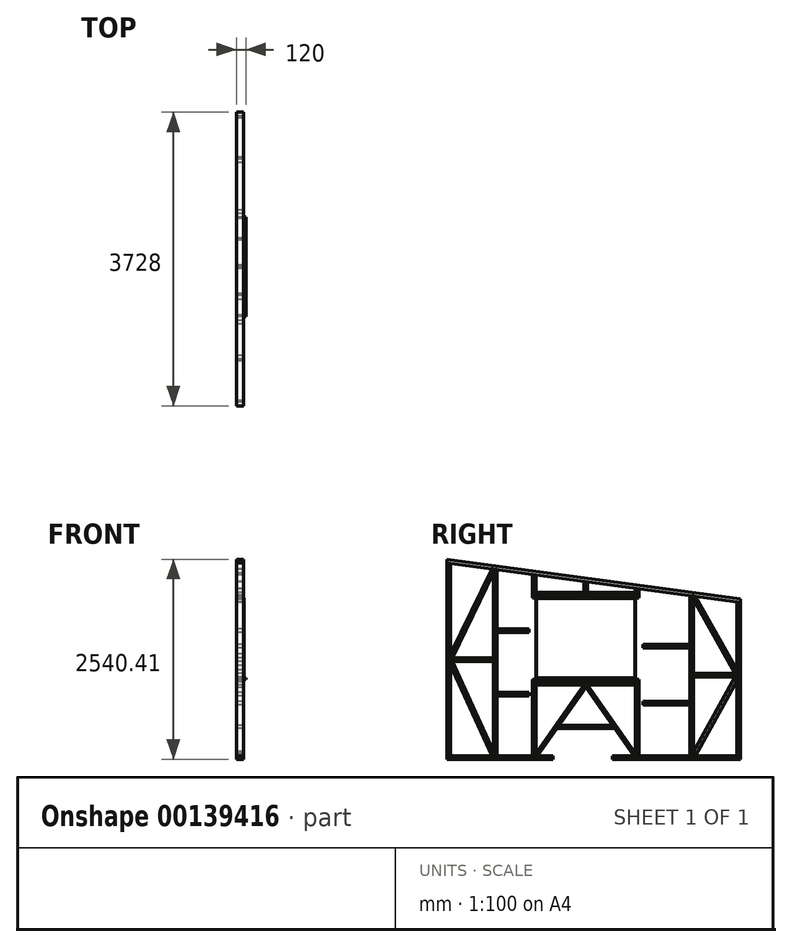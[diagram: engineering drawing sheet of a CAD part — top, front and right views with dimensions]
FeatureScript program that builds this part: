
annotation { "Feature Type Name" : "Feature", "Feature Type Description" : "" }
export const myFeature = defineFeature(function(context is Context, id is Id, definition is map)
    precondition{}
    {
        {
            var Q0;
            Q0=qCreatedBy(makeId("Right.planeOp"),FACE);
            var sketch = newSketch(context, id + "F0", { "sketchPlane" : qUnion([Q0])});
            skLineSegment(sketch, "E0.right", {"start": v(3252.07, -1561.25) * mm, "end": v(3252.07, 393.75) * mm});
            skLineSegment(sketch, "E1", {"start": v(3252.07, 393.75) * mm, "end": v(3297.07, 387.7) * mm});
            skLineSegment(sketch, "E2", {"start": v(3297.07, 387.7) * mm, "end": v(3297.07, -1561.25) * mm});
            skLineSegment(sketch, "E3", {"start": v(164.07, 808.78) * mm, "end": v(164.07, -1561.25) * mm});
            skLineSegment(sketch, "E4", {"start": v(610.07, -1561.25) * mm, "end": v(610.07, 748.84) * mm});
            skLineSegment(sketch, "E5", {"start": v(655.07, -1561.25) * mm, "end": v(655.07, 742.8) * mm});
            skLineSegment(sketch, "E6", {"start": v(610.07, 748.84) * mm, "end": v(655.07, 742.8) * mm});
            skLineSegment(sketch, "E7", {"start": v(2057.07, -1561.25) * mm, "end": v(2057.07, 554.36) * mm});
            skLineSegment(sketch, "E8", {"start": v(2012.07, -1561.25) * mm, "end": v(2012.07, 560.41) * mm});
            skLineSegment(sketch, "E9", {"start": v(2012.07, 560.41) * mm, "end": v(2057.07, 554.36) * mm});
            skLineSegment(sketch, "E10.bottom", {"start": v(655.07, 445.75) * mm, "end": v(2012.07, 445.75) * mm});
            skLineSegment(sketch, "E10.top", {"start": v(655.07, -591.25) * mm, "end": v(2012.07, -591.25) * mm});
            skLineSegment(sketch, "E10.left", {"start": v(655.07, 445.75) * mm, "end": v(655.07, -591.25) * mm});
            skLineSegment(sketch, "E10.right", {"start": v(2012.07, 445.75) * mm, "end": v(2012.07, -591.25) * mm});
            skLineSegment(sketch, "E11", {"start": v(655.07, 480.75) * mm, "end": v(2012.07, 480.75) * mm});
            skLineSegment(sketch, "E12", {"start": v(655.07, -626.25) * mm, "end": v(2012.07, -626.25) * mm});
            skLineSegment(sketch, "E13", {"start": v(655.07, -661.25) * mm, "end": v(2012.07, -661.25) * mm});
            skLineSegment(sketch, "E14", {"start": v(655.07, 515.75) * mm, "end": v(2012.07, 515.75) * mm});
            skPoint(sketch, "E15", {"position": v(1333.57, -661.25) * mm});
            skLineSegment(sketch, "E16", {"start": v(1333.57, -661.25) * mm, "end": v(1333.57, -1561.25) * mm, "construction": true});
            skLineSegment(sketch, "E17", {"start": v(1333.57, -661.25) * mm, "end": v(700.07, -1561.25) * mm, "construction": true});
            skLineSegment(sketch, "E18", {"start": v(1333.57, -661.25) * mm, "end": v(1967.07, -1561.25) * mm, "construction": true});
            skLineSegment(sketch, "E19.right", {"start": v(3297.07, -1561.25) * mm, "end": v(3297.07, -1606.25) * mm});
            skLineSegment(sketch, "E20", {"start": v(-385.93, -361.25) * mm, "end": v(164.07, -1561.25) * mm, "construction": true});
            skLineSegment(sketch, "E21", {"start": v(-361.18, -361.25) * mm, "end": v(164.07, -1507.25) * mm});
            skLineSegment(sketch, "E22", {"start": v(-385.93, -415.25) * mm, "end": v(139.32, -1561.25) * mm});
            skLineSegment(sketch, "E23", {"start": v(3297.07, 387.7) * mm, "end": v(-430.93, 888.75) * mm});
            skLineSegment(sketch, "E24", {"start": v(-430.93, 888.75) * mm, "end": v(-430.93, -1561.25) * mm});
            skLineSegment(sketch, "E25", {"start": v(-430.93, 888.75) * mm, "end": v(-430.93, 934.16) * mm});
            skLineSegment(sketch, "E26", {"start": v(-430.93, 934.16) * mm, "end": v(3297.07, 433.1) * mm});
            skLineSegment(sketch, "E27", {"start": v(3297.07, 433.1) * mm, "end": v(3297.07, 387.7) * mm});
            skLineSegment(sketch, "E28", {"start": v(164.07, -361.25) * mm, "end": v(-385.93, -361.25) * mm});
            skLineSegment(sketch, "E29", {"start": v(164.07, 808.78) * mm, "end": v(-385.93, -316.25) * mm, "construction": true});
            skLineSegment(sketch, "E30", {"start": v(140.57, 811.94) * mm, "end": v(-385.93, -265.02) * mm});
            skLineSegment(sketch, "E31", {"start": v(164.07, 757.55) * mm, "end": v(-360.89, -316.25) * mm});
            skLineSegment(sketch, "E32", {"start": v(2702.07, 467.67) * mm, "end": v(3252.07, -516.25) * mm, "construction": true});
            skLineSegment(sketch, "E33", {"start": v(3252.07, -561.25) * mm, "end": v(2702.07, -1561.25) * mm, "construction": true});
            skLineSegment(sketch, "E34", {"start": v(2729.94, 463.93) * mm, "end": v(3252.07, -470.13) * mm});
            skLineSegment(sketch, "E35", {"start": v(3226.39, -561.25) * mm, "end": v(2702.07, -1514.56) * mm});
            skLineSegment(sketch, "E36", {"start": v(3252.07, -607.94) * mm, "end": v(2727.75, -1561.25) * mm});
            skLineSegment(sketch, "E37", {"start": v(2702.07, -516.25) * mm, "end": v(3252.07, -516.25) * mm});
            skLineSegment(sketch, "E38", {"start": v(2702.07, -561.25) * mm, "end": v(3252.07, -561.25) * mm});
            skLineSegment(sketch, "E39", {"start": v(700.07, -591.25) * mm, "end": v(700.07, 445.75) * mm});
            skLineSegment(sketch, "E40", {"start": v(700.07, 515.75) * mm, "end": v(700.07, 736.74) * mm});
            skLineSegment(sketch, "E41", {"start": v(1967.07, -591.25) * mm, "end": v(1967.07, 445.75) * mm});
            skLineSegment(sketch, "E42", {"start": v(1967.07, 515.75) * mm, "end": v(1967.07, 566.46) * mm});
            skLineSegment(sketch, "E43", {"start": v(1672.07, -1561.25) * mm, "end": v(1672.07, -1606.25) * mm});
            skLineSegment(sketch, "E44", {"start": v(-430.93, -1561.25) * mm, "end": v(919.07, -1561.25) * mm});
            skLineSegment(sketch, "E45", {"start": v(1672.07, -1606.25) * mm, "end": v(3297.07, -1606.25) * mm});
            skLineSegment(sketch, "E46", {"start": v(3297.07, -1561.25) * mm, "end": v(1672.07, -1561.25) * mm});
            skLineSegment(sketch, "E47", {"start": v(919.07, -1606.25) * mm, "end": v(919.07, -1561.25) * mm});
            skLineSegment(sketch, "E48", {"start": v(3226.3, -516.25) * mm, "end": v(2702.07, 421.56) * mm});
            skLineSegment(sketch, "E49", {"start": v(1967.07, -661.25) * mm, "end": v(1967.07, -1561.25) * mm});
            skLineSegment(sketch, "E50", {"start": v(700.07, -661.25) * mm, "end": v(700.07, -1561.25) * mm});
            skLineSegment(sketch, "E51", {"start": v(1354.97, -661.25) * mm, "end": v(1967.07, -1530.84) * mm});
            skLineSegment(sketch, "E52", {"start": v(1333.57, -691.65) * mm, "end": v(1945.67, -1561.25) * mm});
            skLineSegment(sketch, "E53", {"start": v(1333.57, -691.65) * mm, "end": v(721.47, -1561.25) * mm});
            skLineSegment(sketch, "E54", {"start": v(1312.17, -661.25) * mm, "end": v(700.07, -1530.84) * mm});
            skLineSegment(sketch, "E55", {"start": v(1333.57, -691.65) * mm, "end": v(1333.57, -661.25) * mm});
            skLineSegment(sketch, "E56", {"start": v(-385.93, -1561.25) * mm, "end": v(-385.93, 882.7) * mm});
            skLineSegment(sketch, "E57", {"start": v(164.07, -316.25) * mm, "end": v(-385.93, -316.25) * mm});
            skLineSegment(sketch, "E58", {"start": v(919.07, -1606.25) * mm, "end": v(-430.93, -1606.25) * mm});
            skLineSegment(sketch, "E59", {"start": v(-430.93, -1606.25) * mm, "end": v(-430.93, -1561.25) * mm});
            skLineSegment(sketch, "E60", {"start": v(2657.07, 473.72) * mm, "end": v(2657.07, -1561.25) * mm});
            skLineSegment(sketch, "E61", {"start": v(2702.07, 467.67) * mm, "end": v(2702.07, -1561.25) * mm});
            skLineSegment(sketch, "E62", {"start": v(209.07, 802.74) * mm, "end": v(209.07, -1561.25) * mm});
            skLineSegment(sketch, "E63", {"start": v(2657.07, -192.64) * mm, "end": v(2057.07, -192.64) * mm});
            skLineSegment(sketch, "E64", {"start": v(2657.07, -147.64) * mm, "end": v(2057.07, -147.64) * mm});
            skLineSegment(sketch, "E65", {"start": v(2657.07, -913.64) * mm, "end": v(2057.07, -913.64) * mm});
            skLineSegment(sketch, "E66", {"start": v(2657.07, -868.64) * mm, "end": v(2057.07, -868.64) * mm});
            skLineSegment(sketch, "E67", {"start": v(610.07, -800.25) * mm, "end": v(209.07, -800.25) * mm});
            skLineSegment(sketch, "E68", {"start": v(610.07, -755.25) * mm, "end": v(209.07, -755.25) * mm});
            skLineSegment(sketch, "E69", {"start": v(610.07, 5.75) * mm, "end": v(209.07, 5.75) * mm});
            skLineSegment(sketch, "E70", {"start": v(610.07, 50.75) * mm, "end": v(209.07, 50.75) * mm});
            skLineSegment(sketch, "E71", {"start": v(1333.57, 515.75) * mm, "end": v(1333.57, 651.6) * mm, "construction": true});
            skLineSegment(sketch, "E72", {"start": v(1356.07, 648.58) * mm, "end": v(1356.07, 515.75) * mm});
            skLineSegment(sketch, "E73", {"start": v(1311.07, 654.63) * mm, "end": v(1311.07, 515.75) * mm});
            skLineSegment(sketch, "E74", {"start": v(992.47, -1176.25) * mm, "end": v(1674.67, -1176.25) * mm});
            skLineSegment(sketch, "E75", {"start": v(1699.3, -1211.25) * mm, "end": v(967.83, -1211.25) * mm});
            skLineSegment(sketch, "E76", {"start": v(1333.57, -661.25) * mm, "end": v(1333.57, 1002.43) * mm, "construction": true});
            skLineSegment(sketch, "E77.bottom", {"start": v(1955.07, 431.75) * mm, "end": v(712.07, 431.75) * mm});
            skLineSegment(sketch, "E77.top", {"start": v(1955.07, -566.25) * mm, "end": v(712.07, -566.25) * mm});
            skLineSegment(sketch, "E77.left", {"start": v(1955.07, 431.75) * mm, "end": v(1955.07, -566.25) * mm});
            skLineSegment(sketch, "E77.right", {"start": v(712.07, 431.75) * mm, "end": v(712.07, -566.25) * mm});
            skPoint(sketch, "E77.middle", {"position": v(1333.57, -67.25) * mm});
            skLineSegment(sketch, "E78", {"start": v(700.07, -571.25) * mm, "end": v(1967.07, -571.25) * mm});
            skLineSegment(sketch, "E79", {"start": v(700.07, 436.75) * mm, "end": v(1967.07, 436.75) * mm});
            skLineSegment(sketch, "E80", {"start": v(709.07, -591.25) * mm, "end": v(709.07, 436.75) * mm});
            skLineSegment(sketch, "E81", {"start": v(1958.07, 436.75) * mm, "end": v(1958.07, -571.25) * mm});
            skSolve(sketch);
        }
        {
            var Q0;
            {var subQ0=sQuery(id+"F0.wireOp",EDGE,"E3");var subQ5=sQuery(id+"F0.wireOp",EDGE,"E23");var subQ6=makeQuery(id+"F0.imprint","INTERSECT",VERTEX,{"derivedFrom":[subQ0,subQ5]});Q0=makeQuery(id+"F0.imprint","IMPRINT",FACE,{"disambiguationData":[TD([[makeQuery(id+"F0.imprint","IMPRINT",EDGE,{"disambiguationData":[TD([[subQ6,-1.0]])],"derivedFrom":subQ0}),1.0]])]});}
            var Q1;
            {var subQ0=sQuery(id+"F0.wireOp",EDGE,"E10.right");Q1=makeQuery(id+"F0.imprint","IMPRINT",FACE,{"disambiguationData":[TD([[makeQuery(id+"F0.imprint","IMPRINT",EDGE,{"derivedFrom":subQ0}),1.0]])]});}
            var Q2;
            {var subQ0=sQuery(id+"F0.wireOp",EDGE,"E19.bottom");var subQ5=sQuery(id+"F0.wireOp",EDGE,"f47dd481-e89d-4789-ba86-61e8c564b81a");var subQ9=makeQuery(id+"F0.imprint","INTERSECT",VERTEX,{"derivedFrom":[subQ5,subQ0]});Q2=makeQuery(id+"F0.imprint","IMPRINT",FACE,{"disambiguationData":[TD([[makeQuery(id+"F0.imprint","IMPRINT",EDGE,{"disambiguationData":[TD([[subQ9,-1.0]])],"derivedFrom":subQ5}),1.0]])]});}
            var Q3;
            {var subQ0=sQuery(id+"F0.wireOp",EDGE,"9458f50f-a9ba-4b11-8554-c1f147fb82af");var subQ3=sQuery(id+"F0.wireOp",EDGE,"E23");var subQ9=makeQuery(id+"F0.imprint","INTERSECT",VERTEX,{"derivedFrom":[subQ0,subQ3]});Q3=makeQuery(id+"F0.imprint","IMPRINT",FACE,{"disambiguationData":[TD([[makeQuery(id+"F0.imprint","IMPRINT",EDGE,{"disambiguationData":[TD([[subQ9,-1.0]])],"derivedFrom":subQ0}),-1.0]])]});}
            var Q4;
            {var subQ8=sQuery(id+"F0.wireOp",EDGE,"E1");Q4=makeQuery(id+"F0.imprint","IMPRINT",FACE,{"disambiguationData":[TD([[makeQuery(id+"F0.imprint","IMPRINT",EDGE,{"derivedFrom":subQ8}),-1.0]])]});}
            var Q5;
            {var subQ0=sQuery(id+"F0.wireOp",EDGE,"E60");var subQ8=sQuery(id+"F0.wireOp",EDGE,"E23");var subQ11=makeQuery(id+"F0.imprint","INTERSECT",VERTEX,{"derivedFrom":[subQ8,subQ0]});Q5=makeQuery(id+"F0.imprint","IMPRINT",FACE,{"disambiguationData":[TD([[makeQuery(id+"F0.imprint","IMPRINT",EDGE,{"disambiguationData":[TD([[subQ11,1.0]])],"derivedFrom":subQ8}),1.0]])]});}
            var Q6;
            {var subQ0=sQuery(id+"F0.wireOp",EDGE,"qufnCjFI-fICh-2xJd-mXJg-Tk57APwGPwlv");Q6=makeQuery(id+"F0.imprint","IMPRINT",FACE,{"disambiguationData":[TD([[makeQuery(id+"F0.imprint","IMPRINT",EDGE,{"derivedFrom":subQ0}),1.0]])]});}
            var Q7;
            {var subQ0=sQuery(id+"F0.wireOp",EDGE,"E72");Q7=makeQuery(id+"F0.imprint","IMPRINT",FACE,{"disambiguationData":[TD([[makeQuery(id+"F0.imprint","IMPRINT",EDGE,{"derivedFrom":subQ0}),-1.0]])]});}
            var Q8;
            {var subQ6=sQuery(id+"F0.wireOp",EDGE,"E2");Q8=makeQuery(id+"F0.imprint","IMPRINT",FACE,{"disambiguationData":[TD([[makeQuery(id+"F0.imprint","IMPRINT",EDGE,{"derivedFrom":subQ6}),-1.0]])]});}
            var Q9;
            {var subQ6=sQuery(id+"F0.wireOp",EDGE,"E10.left");Q9=makeQuery(id+"F0.imprint","IMPRINT",FACE,{"disambiguationData":[TD([[makeQuery(id+"F0.imprint","IMPRINT",EDGE,{"derivedFrom":subQ6}),-1.0]])]});}
            var Q10;
            {var subQ0=sQuery(id+"F0.wireOp",EDGE,"E74");Q10=makeQuery(id+"F0.imprint","IMPRINT",FACE,{"disambiguationData":[TD([[makeQuery(id+"F0.imprint","IMPRINT",EDGE,{"derivedFrom":subQ0}),-1.0]])]});}
            extrude(context, id + "F1", {"entities" : qUnion([Q0, Q1, Q2, Q3, Q4, Q5, Q6, Q7, Q8, Q9, Q10]), "depth" : 90 * mm});
        }
        {
            var Q0;
            {var subQ0=sQuery(id+"F0.wireOp",EDGE,"KPTtf08t-VQN6-3Sqd-dzWE-HS9itD71kze6");Q0=makeQuery(id+"F0.imprint","IMPRINT",FACE,{"disambiguationData":[TD([[makeQuery(id+"F0.imprint","IMPRINT",EDGE,{"derivedFrom":subQ0}),-1.0]])]});}
            var Q1;
            {var subQ7=sQuery(id+"F0.wireOp",EDGE,"E25");Q1=makeQuery(id+"F0.imprint","IMPRINT",FACE,{"disambiguationData":[TD([[makeQuery(id+"F0.imprint","IMPRINT",EDGE,{"derivedFrom":subQ7}),-1.0]])]});}
            var Q2;
            Q2=makeQuery(id+"F0.imprint","IMPRINT",FACE,{"disambiguationData":[TD([[makeQuery(id+"F0.imprint","IMPRINT",EDGE,{"derivedFrom":sQuery(id+"F0.wireOp",EDGE,"E19.top")}),1.0]])]});
            var Q3;
            {var subQ0=sQuery(id+"F0.wireOp",EDGE,"64f86141-53e5-40fa-8328-e75aae3fffb5");Q3=makeQuery(id+"F0.imprint","IMPRINT",FACE,{"disambiguationData":[TD([[makeQuery(id+"F0.imprint","IMPRINT",EDGE,{"derivedFrom":subQ0}),1.0]])]});}
            var Q4;
            {var subQ0=sQuery(id+"F0.wireOp",EDGE,"E11");Q4=makeQuery(id+"F0.imprint","IMPRINT",FACE,{"disambiguationData":[TD([[makeQuery(id+"F0.imprint","IMPRINT",EDGE,{"derivedFrom":subQ0}),1.0]])]});}
            var Q5;
            {var subQ0=sQuery(id+"F0.wireOp",EDGE,"9b8bf4e2-eade-4215-bfc9-b225c43cc35f");Q5=makeQuery(id+"F0.imprint","IMPRINT",FACE,{"disambiguationData":[TD([[makeQuery(id+"F0.imprint","IMPRINT",EDGE,{"derivedFrom":subQ0}),-1.0]])]});}
            var Q6;
            {var subQ0=sQuery(id+"F0.wireOp",EDGE,"E10.top");Q6=makeQuery(id+"F0.imprint","IMPRINT",FACE,{"disambiguationData":[TD([[makeQuery(id+"F0.imprint","IMPRINT",EDGE,{"derivedFrom":subQ0}),-1.0]])]});}
            var Q7;
            {var subQ0=sQuery(id+"F0.wireOp",EDGE,"7c9494a1-e9da-4e44-a7bb-cec75999e9ff");Q7=makeQuery(id+"F0.imprint","IMPRINT",FACE,{"disambiguationData":[TD([[makeQuery(id+"F0.imprint","IMPRINT",EDGE,{"derivedFrom":subQ0}),1.0]])]});}
            var Q8;
            {var subQ6=sQuery(id+"F0.wireOp",EDGE,"E19.left");Q8=makeQuery(id+"F0.imprint","IMPRINT",FACE,{"disambiguationData":[TD([[makeQuery(id+"F0.imprint","IMPRINT",EDGE,{"derivedFrom":subQ6}),1.0]])]});}
            var Q9;
            {var subQ8=sQuery(id+"F0.wireOp",EDGE,"E19.right");Q9=makeQuery(id+"F0.imprint","IMPRINT",FACE,{"disambiguationData":[TD([[makeQuery(id+"F0.imprint","IMPRINT",EDGE,{"derivedFrom":subQ8}),-1.0]])]});}
            extrude(context, id + "F2", {"entities" : qUnion([Q0, Q1, Q2, Q3, Q4, Q5, Q6, Q7, Q8, Q9]), "depth" : 90 * mm});
        }
        {
            var Q0;
            {var subQ0=sQuery(id+"F0.wireOp",EDGE,"KPTtf08t-VQN6-3Sqd-dzWE-HS9itD71kze6");Q0=makeQuery(id+"F0.imprint","IMPRINT",FACE,{"disambiguationData":[TD([[makeQuery(id+"F0.imprint","IMPRINT",EDGE,{"derivedFrom":subQ0}),-1.0]])]});}
            var Q1;
            {var subQ1=sQuery(id+"F0.wireOp",EDGE,"b06b997c-b915-481a-8fbe-b183472a885f");Q1=makeQuery(id+"F0.imprint","IMPRINT",FACE,{"disambiguationData":[TD([[makeQuery(id+"F0.imprint","IMPRINT",EDGE,{"derivedFrom":subQ1}),-1.0]])]});}
            var Q2;
            {var subQ0=sQuery(id+"F0.wireOp",EDGE,"E10.bottom");Q2=makeQuery(id+"F0.imprint","IMPRINT",FACE,{"disambiguationData":[TD([[makeQuery(id+"F0.imprint","IMPRINT",EDGE,{"derivedFrom":subQ0}),1.0]])]});}
            var Q3;
            {var subQ1=sQuery(id+"F0.wireOp",EDGE,"E21");Q3=makeQuery(id+"F0.imprint","IMPRINT",FACE,{"disambiguationData":[TD([[makeQuery(id+"F0.imprint","IMPRINT",EDGE,{"derivedFrom":subQ1}),-1.0]])]});}
            var Q4;
            {var subQ4=sQuery(id+"F0.wireOp",EDGE,"E5");var subQ6=sQuery(id+"F0.wireOp",EDGE,"E19.bottom");var subQ8=makeQuery(id+"F0.imprint","INTERSECT",VERTEX,{"derivedFrom":[subQ4,subQ6]});Q4=makeQuery(id+"F0.imprint","IMPRINT",FACE,{"disambiguationData":[TD([[makeQuery(id+"F0.imprint","IMPRINT",EDGE,{"disambiguationData":[TD([[subQ8,-1.0]])],"derivedFrom":subQ4}),-1.0]])]});}
            var Q5;
            {var subQ5=sQuery(id+"F0.wireOp",EDGE,"E40");Q5=makeQuery(id+"F0.imprint","IMPRINT",FACE,{"disambiguationData":[TD([[makeQuery(id+"F0.imprint","IMPRINT",EDGE,{"derivedFrom":subQ5}),1.0]])]});}
            var Q6;
            {var subQ5=sQuery(id+"F0.wireOp",EDGE,"E42");Q6=makeQuery(id+"F0.imprint","IMPRINT",FACE,{"disambiguationData":[TD([[makeQuery(id+"F0.imprint","IMPRINT",EDGE,{"derivedFrom":subQ5}),-1.0]])]});}
            var Q7;
            {var subQ2=sQuery(id+"F0.wireOp",EDGE,"E44");var subQ5=sQuery(id+"F0.wireOp",EDGE,"E5");var subQ8=makeQuery(id+"F0.imprint","INTERSECT",VERTEX,{"derivedFrom":[subQ5,subQ2]});Q7=makeQuery(id+"F0.imprint","IMPRINT",FACE,{"disambiguationData":[TD([[makeQuery(id+"F0.imprint","IMPRINT",EDGE,{"disambiguationData":[TD([[subQ8,-1.0]])],"derivedFrom":subQ5}),-1.0]])]});}
            var Q8;
            {var subQ0=sQuery(id+"F0.wireOp",EDGE,"E51");Q8=makeQuery(id+"F0.imprint","IMPRINT",FACE,{"disambiguationData":[TD([[makeQuery(id+"F0.imprint","IMPRINT",EDGE,{"derivedFrom":subQ0}),-1.0]])]});}
            var Q9;
            {var subQ4=sQuery(id+"F0.wireOp",EDGE,"E30");Q9=makeQuery(id+"F0.imprint","IMPRINT",FACE,{"disambiguationData":[TD([[makeQuery(id+"F0.imprint","IMPRINT",EDGE,{"derivedFrom":subQ4}),1.0]])]});}
            extrude(context, id + "F3", {"entities" : qUnion([Q0, Q1, Q2, Q3, Q4, Q5, Q6, Q7, Q8, Q9]), "depth" : 90 * mm});
        }
        {
            var Q0;
            {var subQ4=sQuery(id+"F0.wireOp",EDGE,"E12");Q0=makeQuery(id+"F0.imprint","IMPRINT",FACE,{"disambiguationData":[TD([[makeQuery(id+"F0.imprint","IMPRINT",EDGE,{"derivedFrom":subQ4}),-1.0]])]});}
            var Q1;
            {var subQ0=sQuery(id+"F0.wireOp",EDGE,"dfa8823a-b296-4ffa-9e53-7970a5b6a119");Q1=makeQuery(id+"F0.imprint","IMPRINT",FACE,{"disambiguationData":[TD([[makeQuery(id+"F0.imprint","IMPRINT",EDGE,{"derivedFrom":subQ0}),1.0]])]});}
            var Q2;
            {var subQ4=sQuery(id+"F0.wireOp",EDGE,"9ef19b32-0979-4967-9376-d76fe69ef129");Q2=makeQuery(id+"F0.imprint","IMPRINT",FACE,{"disambiguationData":[TD([[makeQuery(id+"F0.imprint","IMPRINT",EDGE,{"derivedFrom":subQ4}),1.0]])]});}
            var Q3;
            {var subQ0=sQuery(id+"F0.wireOp",EDGE,"6ade3835-2d82-4718-8686-81fffa9f8cbc");Q3=makeQuery(id+"F0.imprint","IMPRINT",FACE,{"disambiguationData":[TD([[makeQuery(id+"F0.imprint","IMPRINT",EDGE,{"derivedFrom":subQ0}),1.0]])]});}
            var Q4;
            {var subQ3=sQuery(id+"F0.wireOp",EDGE,"5245ddd8-1579-4c4f-af40-db80d6400164");Q4=makeQuery(id+"F0.imprint","IMPRINT",FACE,{"disambiguationData":[TD([[makeQuery(id+"F0.imprint","IMPRINT",EDGE,{"derivedFrom":subQ3}),1.0]])]});}
            var Q5;
            {var subQ7=sQuery(id+"F0.wireOp",EDGE,"RlIxCtcS-trtu-WQvO-zQgg-4jTADaSzlUrx");Q5=makeQuery(id+"F0.imprint","IMPRINT",FACE,{"disambiguationData":[TD([[makeQuery(id+"F0.imprint","IMPRINT",EDGE,{"derivedFrom":subQ7}),-1.0]])]});}
            var Q6;
            {var subQ0=sQuery(id+"F0.wireOp",EDGE,"CYmrAsSX-5kBQ-Xpl4-JUuo-22nQuxJc7QHB");Q6=makeQuery(id+"F0.imprint","IMPRINT",FACE,{"disambiguationData":[TD([[makeQuery(id+"F0.imprint","IMPRINT",EDGE,{"derivedFrom":subQ0}),1.0]])]});}
            var Q7;
            {var subQ0=sQuery(id+"F0.wireOp",EDGE,"E37");Q7=makeQuery(id+"F0.imprint","IMPRINT",FACE,{"disambiguationData":[TD([[makeQuery(id+"F0.imprint","IMPRINT",EDGE,{"derivedFrom":subQ0}),-1.0]])]});}
            var Q8;
            {var subQ0=sQuery(id+"F0.wireOp",EDGE,"E28");Q8=makeQuery(id+"F0.imprint","IMPRINT",FACE,{"disambiguationData":[TD([[makeQuery(id+"F0.imprint","IMPRINT",EDGE,{"derivedFrom":subQ0}),-1.0]])]});}
            var Q9;
            {var subQ0=sQuery(id+"F0.wireOp",EDGE,"E10.left");Q9=makeQuery(id+"F0.imprint","IMPRINT",FACE,{"disambiguationData":[TD([[makeQuery(id+"F0.imprint","IMPRINT",EDGE,{"derivedFrom":subQ0}),1.0]])]});}
            var Q10;
            {var subQ0=sQuery(id+"F0.wireOp",EDGE,"E10.right");Q10=makeQuery(id+"F0.imprint","IMPRINT",FACE,{"disambiguationData":[TD([[makeQuery(id+"F0.imprint","IMPRINT",EDGE,{"derivedFrom":subQ0}),-1.0]])]});}
            var Q11;
            Q11=makeQuery(id+"F0.imprint","IMPRINT",FACE,{"disambiguationData":[TD([[makeQuery(id+"F0.imprint","IMPRINT",EDGE,{"derivedFrom":sQuery(id+"F0.wireOp",EDGE,"leANnIw1-Praa-n9E5-XdZE-SoG3ZTwqAIro")}),1.0]])]});
            var Q12;
            {var subQ7=sQuery(id+"F0.wireOp",EDGE,"E43");Q12=makeQuery(id+"F0.imprint","IMPRINT",FACE,{"disambiguationData":[TD([[makeQuery(id+"F0.imprint","IMPRINT",EDGE,{"derivedFrom":subQ7}),1.0]])]});}
            var Q13;
            {var subQ5=sQuery(id+"F0.wireOp",EDGE,"E47");Q13=makeQuery(id+"F0.imprint","IMPRINT",FACE,{"disambiguationData":[TD([[makeQuery(id+"F0.imprint","IMPRINT",EDGE,{"derivedFrom":subQ5}),1.0]])]});}
            extrude(context, id + "F4", {"entities" : qUnion([Q0, Q1, Q2, Q3, Q4, Q5, Q6, Q7, Q8, Q9, Q10, Q11, Q12, Q13]), "depth" : 90 * mm});
        }
        {
            var Q0;
            {var subQ1=sQuery(id+"F0.wireOp",EDGE,"bf5e6e2e-78c9-4953-b28f-61fd8f0e8776");Q0=makeQuery(id+"F0.imprint","IMPRINT",FACE,{"disambiguationData":[TD([[makeQuery(id+"F0.imprint","IMPRINT",EDGE,{"derivedFrom":subQ1}),1.0]])]});}
            var Q1;
            {var subQ7=sQuery(id+"F0.wireOp",EDGE,"E24");Q1=makeQuery(id+"F0.imprint","IMPRINT",FACE,{"disambiguationData":[TD([[makeQuery(id+"F0.imprint","IMPRINT",EDGE,{"derivedFrom":subQ7}),1.0]])]});}
            var Q2;
            {var subQ0=sQuery(id+"F0.wireOp",EDGE,"E34");Q2=makeQuery(id+"F0.imprint","IMPRINT",FACE,{"disambiguationData":[TD([[makeQuery(id+"F0.imprint","IMPRINT",EDGE,{"derivedFrom":subQ0}),-1.0]])]});}
            var Q3;
            {var subQ0=sQuery(id+"F0.wireOp",EDGE,"E35");Q3=makeQuery(id+"F0.imprint","IMPRINT",FACE,{"disambiguationData":[TD([[makeQuery(id+"F0.imprint","IMPRINT",EDGE,{"derivedFrom":subQ0}),1.0]])]});}
            var Q4;
            {var subQ0=sQuery(id+"F0.wireOp",EDGE,"E19.bottom");var subQ1=sQuery(id+"F0.wireOp",EDGE,"E8");var subQ2=makeQuery(id+"F0.imprint","INTERSECT",VERTEX,{"derivedFrom":[subQ1,subQ0]});Q4=makeQuery(id+"F0.imprint","IMPRINT",FACE,{"disambiguationData":[TD([[makeQuery(id+"F0.imprint","IMPRINT",EDGE,{"disambiguationData":[TD([[subQ2,-1.0]])],"derivedFrom":subQ1}),1.0]])]});}
            var Q5;
            {var subQ4=sQuery(id+"F0.wireOp",EDGE,"E46");var subQ6=sQuery(id+"F0.wireOp",EDGE,"E8");var subQ8=makeQuery(id+"F0.imprint","INTERSECT",VERTEX,{"derivedFrom":[subQ6,subQ4]});Q5=makeQuery(id+"F0.imprint","IMPRINT",FACE,{"disambiguationData":[TD([[makeQuery(id+"F0.imprint","IMPRINT",EDGE,{"disambiguationData":[TD([[subQ8,-1.0]])],"derivedFrom":subQ6}),1.0]])]});}
            var Q6;
            {var subQ0=sQuery(id+"F0.wireOp",EDGE,"E53");Q6=makeQuery(id+"F0.imprint","IMPRINT",FACE,{"disambiguationData":[TD([[makeQuery(id+"F0.imprint","IMPRINT",EDGE,{"derivedFrom":subQ0}),-1.0]])]});}
            var Q7;
            {var subQ0=sQuery(id+"F0.wireOp",EDGE,"jz2GwP5B-BYwh-5LA0-e6QM-Q7ma7MhSX5sU");Q7=makeQuery(id+"F0.imprint","IMPRINT",FACE,{"disambiguationData":[TD([[makeQuery(id+"F0.imprint","IMPRINT",EDGE,{"derivedFrom":subQ0}),1.0]])]});}
            var Q8;
            {var subQ0=sQuery(id+"F0.wireOp",EDGE,"U7ykKrcy-WcKr-67Zd-qoY2-V05vreiuqBrm");Q8=makeQuery(id+"F0.imprint","IMPRINT",FACE,{"disambiguationData":[TD([[makeQuery(id+"F0.imprint","IMPRINT",EDGE,{"derivedFrom":subQ0}),1.0]])]});}
            var Q9;
            {var subQ0=sQuery(id+"F0.wireOp",EDGE,"E65");Q9=makeQuery(id+"F0.imprint","IMPRINT",FACE,{"disambiguationData":[TD([[makeQuery(id+"F0.imprint","IMPRINT",EDGE,{"derivedFrom":subQ0}),-1.0]])]});}
            var Q10;
            {var subQ0=sQuery(id+"F0.wireOp",EDGE,"E63");Q10=makeQuery(id+"F0.imprint","IMPRINT",FACE,{"disambiguationData":[TD([[makeQuery(id+"F0.imprint","IMPRINT",EDGE,{"derivedFrom":subQ0}),-1.0]])]});}
            var Q11;
            {var subQ0=sQuery(id+"F0.wireOp",EDGE,"E69");Q11=makeQuery(id+"F0.imprint","IMPRINT",FACE,{"disambiguationData":[TD([[makeQuery(id+"F0.imprint","IMPRINT",EDGE,{"derivedFrom":subQ0}),-1.0]])]});}
            var Q12;
            {var subQ0=sQuery(id+"F0.wireOp",EDGE,"E67");Q12=makeQuery(id+"F0.imprint","IMPRINT",FACE,{"disambiguationData":[TD([[makeQuery(id+"F0.imprint","IMPRINT",EDGE,{"derivedFrom":subQ0}),-1.0]])]});}
            var Q13;
            {var subQ0=sQuery(id+"F0.wireOp",EDGE,"lduWqaPK-swWl-ufKk-uTi5-J9pPSfNxhEaR");Q13=makeQuery(id+"F0.imprint","IMPRINT",FACE,{"disambiguationData":[TD([[makeQuery(id+"F0.imprint","IMPRINT",EDGE,{"derivedFrom":subQ0}),-1.0]])]});}
            extrude(context, id + "F5", {"entities" : qUnion([Q0, Q1, Q2, Q3, Q4, Q5, Q6, Q7, Q8, Q9, Q10, Q11, Q12, Q13]), "depth" : 90 * mm});
        }
        {
            var Q0;
            {var subQ0=sQuery(id+"F0.wireOp",EDGE,"E78");var subQ1=sQuery(id+"F0.wireOp",EDGE,"E39");var subQ2=makeQuery(id+"F0.imprint","INTERSECT",VERTEX,{"derivedFrom":[subQ1,subQ0]});Q0=makeQuery(id+"F0.imprint","IMPRINT",FACE,{"disambiguationData":[TD([[makeQuery(id+"F0.imprint","IMPRINT",EDGE,{"disambiguationData":[TD([[subQ2,-1.0]])],"derivedFrom":subQ1}),-1.0]])]});}
            var Q1;
            {var subQ5=sQuery(id+"F0.wireOp",EDGE,"E81");Q1=makeQuery(id+"F0.imprint","IMPRINT",FACE,{"disambiguationData":[TD([[makeQuery(id+"F0.imprint","IMPRINT",EDGE,{"derivedFrom":subQ5}),1.0]])]});}
            extrude(context, id + "F6", {"entities" : qUnion([Q0, Q1]), "depth" : 100 * mm});
        }
        {
            var Q0;
            {var subQ1=sQuery(id+"F0.wireOp",EDGE,"E39");var subQ5=sQuery(id+"F0.wireOp",EDGE,"E10.bottom");var subQ8=makeQuery(id+"F0.imprint","INTERSECT",VERTEX,{"derivedFrom":[subQ5,subQ1]});Q0=makeQuery(id+"F0.imprint","IMPRINT",FACE,{"disambiguationData":[TD([[makeQuery(id+"F0.imprint","IMPRINT",EDGE,{"disambiguationData":[TD([[subQ8,-1.0]])],"derivedFrom":subQ5}),-1.0]])]});}
            extrude(context, id + "F7", {"entities" : qUnion([Q0]), "depth" : 100 * mm});
        }
        {
            var Q0;
            {var subQ0=sQuery(id+"F0.wireOp",EDGE,"E39");var subQ1=sQuery(id+"F0.wireOp",EDGE,"E10.top");var subQ2=makeQuery(id+"F0.imprint","INTERSECT",VERTEX,{"derivedFrom":[subQ1,subQ0]});Q0=makeQuery(id+"F0.imprint","IMPRINT",FACE,{"disambiguationData":[TD([[makeQuery(id+"F0.imprint","IMPRINT",EDGE,{"disambiguationData":[TD([[subQ2,-1.0]])],"derivedFrom":subQ1}),1.0]])]});}
            var Q1;
            {var subQ1=sQuery(id+"F0.wireOp",EDGE,"E41");var subQ6=sQuery(id+"F0.wireOp",EDGE,"E10.top");var subQ7=makeQuery(id+"F0.imprint","INTERSECT",VERTEX,{"derivedFrom":[subQ6,subQ1]});Q1=makeQuery(id+"F0.imprint","IMPRINT",FACE,{"disambiguationData":[TD([[makeQuery(id+"F0.imprint","IMPRINT",EDGE,{"disambiguationData":[TD([[subQ7,1.0]])],"derivedFrom":subQ6}),1.0]])]});}
            extrude(context, id + "F8", {"entities" : qUnion([Q0, Q1]), "depth" : 120 * mm});
        }
    });
